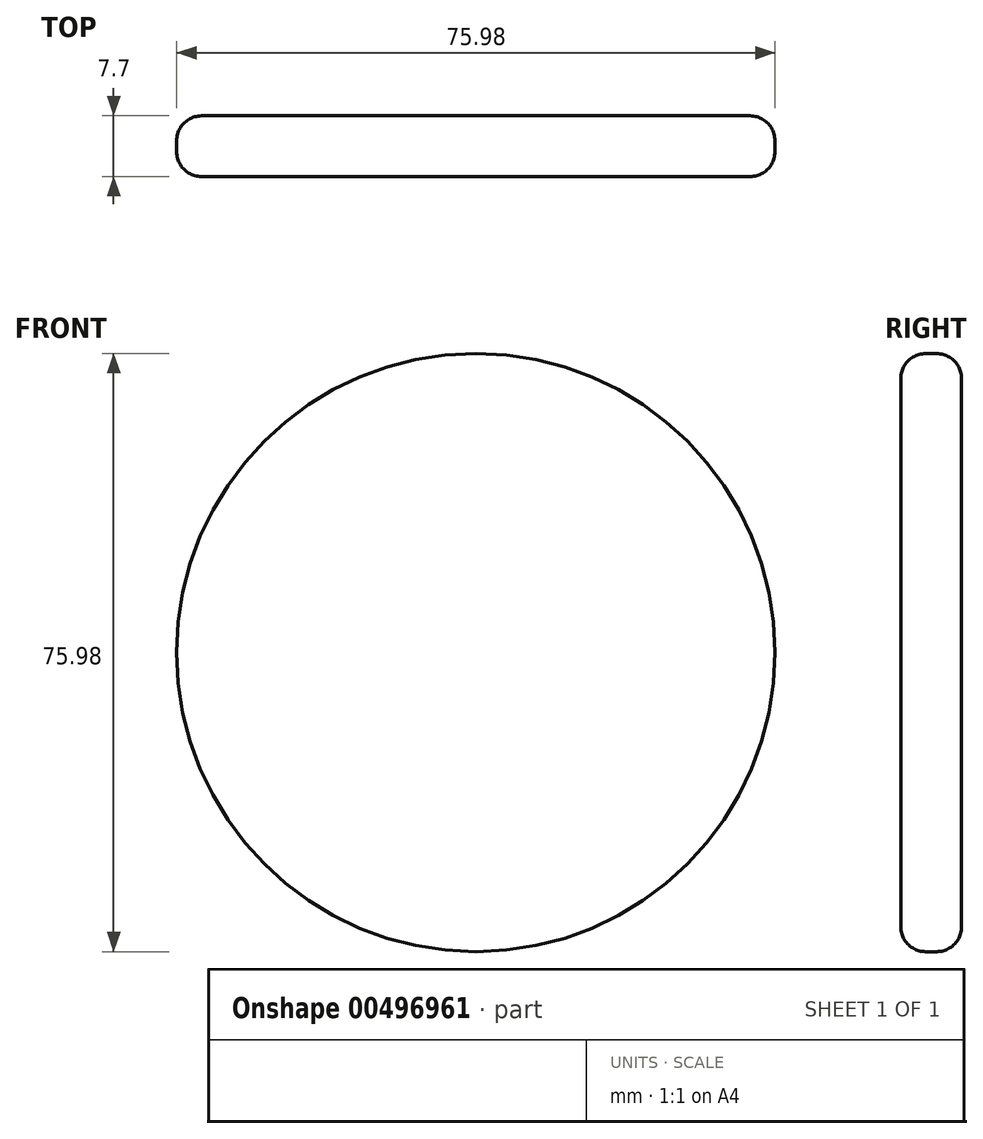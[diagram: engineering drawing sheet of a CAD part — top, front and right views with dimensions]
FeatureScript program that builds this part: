
annotation { "Feature Type Name" : "Feature", "Feature Type Description" : "" }
export const myFeature = defineFeature(function(context is Context, id is Id, definition is map)
    precondition{}
    {
        {
            var Q0;
            Q0=qCreatedBy(makeId("Front.planeOp"),FACE);
            var sketch = newSketch(context, id + "F0", { "sketchPlane" : qUnion([Q0])});
            skCircle(sketch, "E0", {"center": v(0, 0) * mm, "radius": 38 * mm});
            skSolve(sketch);
        }
        {
            var Q0;
            Q0=makeQuery(id+"F0.imprint","IMPRINT",FACE,{"disambiguationData":[TD([[makeQuery(id+"F0.imprint","IMPRINT",EDGE,{"derivedFrom":sQuery(id+"F0.wireOp",EDGE,"E0")}),1.0]])]});
            extrude(context, id + "F1", {"entities" : qUnion([Q0]), "depth" : 7.7 * mm});
        }
        {
            var Q0;
            Q0=makeQuery(id+"F1.opExtrude","SWEPT_FACE",FACE,{"disambiguationData":[OSD([sQuery(id+"F0.wireOp",EDGE,"E0")])]});
            fillet(context, id + "F2", {"entities" : qUnion([Q0]), "radius" : 3.14 * mm, "tangentPropagation" : true, "allowEdgeOverflow" : false});
        }
        {
            var Q0;
            Q0=qCreatedBy(makeId("Front.planeOp"),FACE);
            var sketch = newSketch(context, id + "F3", { "sketchPlane" : qUnion([Q0])});
            skCircle(sketch, "E1", {"center": v(0, 0) * mm, "radius": 17.9 * mm});
            skSolve(sketch);
        }
        {
            var Q0;
            Q0=sQuery(id+"F3.wireOp",EDGE,"E1");
            extrude(context, id + "F4", {"bodyType" : ToolBodyType.SURFACE, "surfaceEntities" : qUnion([Q0]), "depth" : 7.7 * mm});
        }
    });
